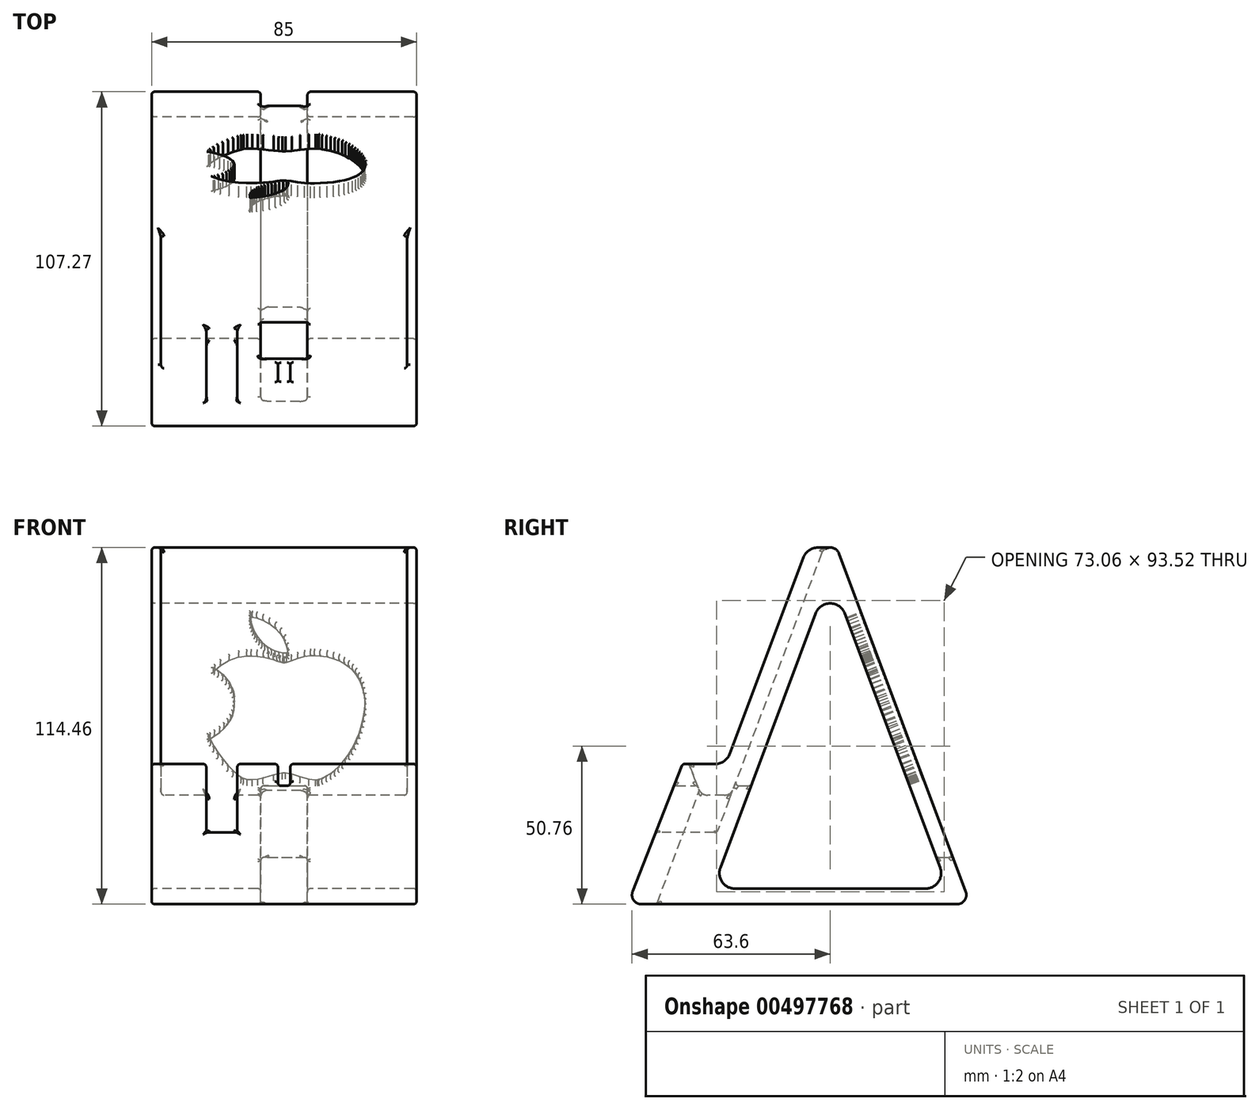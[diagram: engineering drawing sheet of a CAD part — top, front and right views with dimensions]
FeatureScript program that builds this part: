
annotation { "Feature Type Name" : "Feature", "Feature Type Description" : "" }
export const myFeature = defineFeature(function(context is Context, id is Id, definition is map)
    precondition{}
    {
        {
            var Q0;
            Q0=qCreatedBy(makeId("Right.planeOp"),FACE);
            var sketch = newSketch(context, id + "F0", { "sketchPlane" : qUnion([Q0])});
            skLineSegment(sketch, "E0", {"start": v(0, 0) * mm, "end": v(0, 120) * mm, "construction": true});
            skLineSegment(sketch, "E1", {"start": v(0, 0) * mm, "end": v(45, 0) * mm, "construction": true});
            skLineSegment(sketch, "E2", {"start": v(0, 0) * mm, "end": v(-65, 0) * mm, "construction": true});
            skLineSegment(sketch, "E3", {"start": v(-65, 0) * mm, "end": v(-65, 35) * mm, "construction": true});
            skLineSegment(sketch, "E4", {"start": v(2.8, 112.5) * mm, "end": v(43.48, 4.05) * mm});
            skLineSegment(sketch, "E5.MirrorCS", {"start": v(-2.8, 112.5) * mm, "end": v(-31.15, 36.95) * mm});
            skLineSegment(sketch, "E6.0", {"start": v(-16.85, 126.32) * mm, "end": v(-47.35, 45) * mm, "construction": true});
            skLineSegment(sketch, "E7", {"start": v(40.67, 0) * mm, "end": v(-60.6, 0) * mm});
            skLineSegment(sketch, "E8.0", {"start": v(30.57, 5) * mm, "end": v(-30.57, 5) * mm});
            skLineSegment(sketch, "E9.0", {"start": v(4.68, 93.28) * mm, "end": v(35.25, 11.76) * mm});
            skArc(sketch, "E10.filletArc", {"start": v(30.57, 5) * mm, "mid": v(34.68, 7.15) * mm, "end": v(35.25, 11.76) * mm});
            skPoint(sketch, "E11.visualSharp", {"position": v(45, 0) * mm});
            skArc(sketch, "E11.filletArc", {"start": v(40.67, 0) * mm, "mid": v(43.14, 1.3) * mm, "end": v(43.48, 4.05) * mm});
            skPoint(sketch, "E12.visualSharp", {"position": v(0, 120) * mm});
            skArc(sketch, "E12.filletArc", {"start": v(2.8, 112.5) * mm, "mid": v(0, 114.46) * mm, "end": v(-2.8, 112.5) * mm});
            skLineSegment(sketch, "E13.0", {"start": v(-4.68, 93.28) * mm, "end": v(-35.25, 11.76) * mm});
            skArc(sketch, "E14.filletArc", {"start": v(4.68, 93.28) * mm, "mid": v(0, 96.52) * mm, "end": v(-4.68, 93.28) * mm});
            skArc(sketch, "E15.filletArc", {"start": v(-35.25, 11.76) * mm, "mid": v(-34.68, 7.15) * mm, "end": v(-30.57, 5) * mm});
            skLineSegment(sketch, "E16.0", {"start": v(-33.95, 35) * mm, "end": v(-39.38, 35) * mm});
            skPoint(sketch, "E17.orphan", {"position": v(-45, 0) * mm});
            skPoint(sketch, "E18.visualSharp", {"position": v(-31.88, 35) * mm});
            skArc(sketch, "E18.filletArc", {"start": v(-33.95, 35) * mm, "mid": v(-32.25, 35.53) * mm, "end": v(-31.15, 36.95) * mm});
            skLineSegment(sketch, "E19", {"start": v(-47.6, 44.37) * mm, "end": v(-63.4, 4.1) * mm});
            skPoint(sketch, "E20.visualSharp", {"position": v(-65, 0) * mm});
            skArc(sketch, "E20.filletArc", {"start": v(-63.4, 4.1) * mm, "mid": v(-63.08, 1.3) * mm, "end": v(-60.6, 0) * mm});
            skLineSegment(sketch, "E21", {"start": v(-46.67, 45) * mm, "end": v(-46.03, 45) * mm});
            skLineSegment(sketch, "E22", {"start": v(-46.35, 45) * mm, "end": v(-46.35, 35.19) * mm, "construction": true});
            skLineSegment(sketch, "E23.MirrorCS", {"start": v(-45.1, 44.37) * mm, "end": v(-42.17, 36.9) * mm});
            skArc(sketch, "E24.filletArc", {"start": v(-42.17, 36.9) * mm, "mid": v(-41.07, 35.52) * mm, "end": v(-39.38, 35) * mm});
            skPoint(sketch, "E25.visualSharp", {"position": v(-47.35, 45) * mm});
            skArc(sketch, "E25.filletArc", {"start": v(-46.67, 45) * mm, "mid": v(-47.23, 44.83) * mm, "end": v(-47.6, 44.37) * mm});
            skPoint(sketch, "E26.visualSharp", {"position": v(-45.35, 45) * mm});
            skArc(sketch, "E26.filletArc", {"start": v(-45.1, 44.37) * mm, "mid": v(-45.47, 44.83) * mm, "end": v(-46.03, 45) * mm});
            skSolve(sketch);
        }
        {
            var Q0;
            Q0=makeQuery(id+"F0.imprint","IMPRINT",FACE,{"disambiguationData":[TD([[makeQuery(id+"F0.imprint","IMPRINT",EDGE,{"derivedFrom":sQuery(id+"F0.wireOp",EDGE,"E4")}),-1.0]])]});
            extrude(context, id + "F1", {"entities" : qUnion([Q0]), "endBound" : BoundingType.SYMMETRIC, "depth" : 85 * mm});
        }
        {
            var Q0;
            Q0=qCreatedBy(makeId("Right.planeOp"),FACE);
            var sketch = newSketch(context, id + "F2", { "sketchPlane" : qUnion([Q0])});
            skLineSegment(sketch, "E27.0", {"start": v(-4.68, 93.28) * mm, "end": v(-35.25, 11.76) * mm, "construction": true});
            skLineSegment(sketch, "E28.0", {"start": v(-18.73, 98.54) * mm, "end": v(-49.3, 17.02) * mm, "construction": true});
            skLineSegment(sketch, "E29.0", {"start": v(40.67, 0) * mm, "end": v(-60.6, 0) * mm, "construction": true});
            skLineSegment(sketch, "E30.0", {"start": v(40.67, -5) * mm, "end": v(-60.6, -5) * mm, "construction": true});
            skLineSegment(sketch, "E31.0", {"start": v(30.57, 5) * mm, "end": v(-30.57, 5) * mm, "construction": true});
            skLineSegment(sketch, "E32.0", {"start": v(30.57, 15) * mm, "end": v(-30.57, 15) * mm, "construction": true});
            skLineSegment(sketch, "E33", {"start": v(48.4, 22.62) * mm, "end": v(48.4, -8.79) * mm, "construction": true});
            skLineSegment(sketch, "E34.0", {"start": v(-33.95, 35) * mm, "end": v(-39.38, 35) * mm, "construction": true});
            skPoint(sketch, "E34.1", {"position": v(-36.67, 35) * mm});
            skLineSegment(sketch, "E35.0", {"start": v(-33.95, 38) * mm, "end": v(-39.38, 38) * mm, "construction": true});
            skLineSegment(sketch, "E36", {"start": v(-49.3, 17.02) * mm, "end": v(-57.76, -5.55) * mm, "construction": true});
            skLineSegment(sketch, "E37", {"start": v(-33.95, 38) * mm, "end": v(-17.32, 38) * mm, "construction": true});
            skLineSegment(sketch, "E38", {"start": v(-30.57, 15) * mm, "end": v(-21.94, 38) * mm});
            skLineSegment(sketch, "E39", {"start": v(-30.57, 15) * mm, "end": v(48.4, 15) * mm});
            skLineSegment(sketch, "E40", {"start": v(48.4, 15) * mm, "end": v(48.4, -5) * mm});
            skLineSegment(sketch, "E41", {"start": v(48.4, -5) * mm, "end": v(-57.56, -5) * mm});
            skLineSegment(sketch, "E42", {"start": v(-57.56, -5) * mm, "end": v(-41.43, 38) * mm});
            skLineSegment(sketch, "E43", {"start": v(-41.43, 38) * mm, "end": v(-21.94, 38) * mm});
            skSolve(sketch);
        }
        {
            var Q0;
            Q0=makeQuery(id+"F2.imprint","IMPRINT",FACE,{"disambiguationData":[TD([[makeQuery(id+"F2.imprint","IMPRINT",EDGE,{"derivedFrom":sQuery(id+"F2.wireOp",EDGE,"E38")}),1.0]])]});
            extrude(context, id + "F3", {"entities" : qUnion([Q0]), "operationType" : NewBodyOperationType.REMOVE, "endBound" : BoundingType.SYMMETRIC, "depth" : 15 * mm});
        }
        {
            var Q0;
            Q0=qCreatedBy(makeId("Right.planeOp"),FACE);
            cPlane(context, id + "F4", {"entities" : qUnion([Q0]), "cplaneType" : CPlaneType.OFFSET, "offset" : 20 * mm, "oppositeDirection" : true, "width" : 150 * mm, "height" : 150 * mm});
        }
        {
            var Q0;
            Q0=qCreatedBy(id+"F4.planeOp",FACE);
            var sketch = newSketch(context, id + "F5", { "sketchPlane" : qUnion([Q0])});
            skLineSegment(sketch, "E44.0", {"start": v(-33.95, 35) * mm, "end": v(-39.38, 35) * mm, "construction": true});
            skLineSegment(sketch, "E45.0", {"start": v(-33.95, 38) * mm, "end": v(-39.38, 38) * mm, "construction": true});
            skLineSegment(sketch, "E46.0", {"start": v(-33.95, 23) * mm, "end": v(-39.38, 23) * mm, "construction": true});
            skLineSegment(sketch, "E47.0", {"start": v(-2.8, 112.5) * mm, "end": v(-31.15, 36.95) * mm});
            skLineSegment(sketch, "E48", {"start": v(-31.15, 36.95) * mm, "end": v(-36.38, 23) * mm, "construction": true});
            skPoint(sketch, "E48.endSnap0", {"position": v(-36.67, 23) * mm});
            skLineSegment(sketch, "E49", {"start": v(-36.38, 23) * mm, "end": v(-59.4, 23) * mm, "construction": true});
            skLineSegment(sketch, "E50", {"start": v(-59.4, 23) * mm, "end": v(-53.77, 38) * mm, "construction": true});
            skLineSegment(sketch, "E51", {"start": v(-30.75, 38) * mm, "end": v(-31.15, 36.95) * mm, "construction": true});
            skLineSegment(sketch, "E52", {"start": v(-36.38, 23) * mm, "end": v(-59.4, 23) * mm});
            skLineSegment(sketch, "E53", {"start": v(-53.77, 38) * mm, "end": v(-59.4, 23) * mm});
            skLineSegment(sketch, "E54", {"start": v(-30.75, 38) * mm, "end": v(-36.38, 23) * mm});
            skLineSegment(sketch, "E55", {"start": v(-30.75, 38) * mm, "end": v(-39.38, 38) * mm});
            skLineSegment(sketch, "E56", {"start": v(-39.38, 38) * mm, "end": v(-44.36, 49.18) * mm});
            skLineSegment(sketch, "E57", {"start": v(-44.36, 49.18) * mm, "end": v(-50.54, 48.17) * mm});
            skLineSegment(sketch, "E58", {"start": v(-50.54, 48.17) * mm, "end": v(-53.77, 38) * mm});
            skSolve(sketch);
        }
        {
            var Q0;
            {var subQ2=sQuery(id+"F5.wireOp",EDGE,"E52");Q0=makeQuery(id+"F5.imprint","IMPRINT",FACE,{"disambiguationData":[TD([[makeQuery(id+"F5.imprint","IMPRINT",EDGE,{"derivedFrom":subQ2}),-1.0]])]});}
            extrude(context, id + "F6", {"entities" : qUnion([Q0]), "operationType" : NewBodyOperationType.REMOVE, "endBound" : BoundingType.SYMMETRIC, "depth" : 10 * mm});
        }
        {
            var Q0;
            Q0=qCreatedBy(makeId("Front.planeOp"),FACE);
            cPlane(context, id + "F7", {"entities" : qUnion([Q0]), "cplaneType" : CPlaneType.OFFSET, "offset" : 46 * mm, "width" : 150 * mm, "height" : 150 * mm});
        }
        {
            var Q0;
            Q0=qCreatedBy(id+"F7.planeOp",FACE);
            var sketch = newSketch(context, id + "F8", { "sketchPlane" : qUnion([Q0])});
            skLineSegment(sketch, "E59.0", {"start": v(42.5, 45) * mm, "end": v(-15, 45) * mm, "construction": true});
            skLineSegment(sketch, "E60", {"start": v(0, 0) * mm, "end": v(0, 47) * mm, "construction": true});
            skLineSegment(sketch, "E61.0", {"start": v(2, 39) * mm, "end": v(2, 47) * mm});
            skLineSegment(sketch, "E62.0", {"start": v(-2, 39) * mm, "end": v(-2, 47) * mm});
            skLineSegment(sketch, "E63", {"start": v(1, 38) * mm, "end": v(-1, 38) * mm});
            skLineSegment(sketch, "E64", {"start": v(-2, 47) * mm, "end": v(2, 47) * mm});
            skPoint(sketch, "E65.visualSharp", {"position": v(2, 38) * mm});
            skArc(sketch, "E65.filletArc", {"start": v(1, 38) * mm, "mid": v(1.7, 38.3) * mm, "end": v(2, 39) * mm});
            skPoint(sketch, "E66.visualSharp", {"position": v(-2, 38) * mm});
            skArc(sketch, "E66.filletArc", {"start": v(-2, 39) * mm, "mid": v(-1.7, 38.3) * mm, "end": v(-1, 38) * mm});
            skSolve(sketch);
        }
        {
            var Q0;
            Q0=makeQuery(id+"F8.imprint","IMPRINT",FACE,{"disambiguationData":[TD([[makeQuery(id+"F8.imprint","IMPRINT",EDGE,{"derivedFrom":sQuery(id+"F8.wireOp",EDGE,"E61.0")}),1.0]])]});
            extrude(context, id + "F9", {"entities" : qUnion([Q0]), "operationType" : NewBodyOperationType.REMOVE, "endBound" : BoundingType.SYMMETRIC, "depth" : 10 * mm});
        }
        {
            var Q0;
            Q0=makeQuery(id+"F1.opExtrude","SWEPT_FACE",FACE,{"disambiguationData":[OSD([sQuery(id+"F0.wireOp",EDGE,"E4")])]});
            var sketch = newSketch(context, id + "F10", { "sketchPlane" : qUnion([Q0])});
            skLineSegment(sketch, "E67", {"start": v(-10.8, 27.05) * mm, "end": v(-11.15, 27.16) * mm});
            skLineSegment(sketch, "E68", {"start": v(-11.15, 27.16) * mm, "end": v(-12.2, 27.58) * mm});
            skLineSegment(sketch, "E69", {"start": v(-12.2, 27.58) * mm, "end": v(-13.57, 28.3) * mm});
            skLineSegment(sketch, "E70", {"start": v(-13.57, 28.3) * mm, "end": v(-14.9, 29.19) * mm});
            skLineSegment(sketch, "E71", {"start": v(-14.9, 29.19) * mm, "end": v(-16.18, 30.24) * mm});
            skLineSegment(sketch, "E72", {"start": v(-16.18, 30.24) * mm, "end": v(-17.4, 31.45) * mm});
            skLineSegment(sketch, "E73", {"start": v(-17.4, 31.45) * mm, "end": v(-18.58, 32.79) * mm});
            skLineSegment(sketch, "E74", {"start": v(-18.58, 32.79) * mm, "end": v(-19.68, 34.25) * mm});
            skLineSegment(sketch, "E75", {"start": v(-19.68, 34.25) * mm, "end": v(-20.72, 35.82) * mm});
            skLineSegment(sketch, "E76", {"start": v(-20.72, 35.82) * mm, "end": v(-21.68, 37.48) * mm});
            skLineSegment(sketch, "E77", {"start": v(-21.68, 37.48) * mm, "end": v(-22.56, 39.23) * mm});
            skLineSegment(sketch, "E78", {"start": v(-22.56, 39.23) * mm, "end": v(-23.35, 41.05) * mm});
            skLineSegment(sketch, "E79", {"start": v(-23.35, 41.05) * mm, "end": v(-24.04, 42.92) * mm});
            skLineSegment(sketch, "E80", {"start": v(-24.04, 42.92) * mm, "end": v(-24.64, 44.84) * mm});
            skLineSegment(sketch, "E81", {"start": v(-24.64, 44.84) * mm, "end": v(-25.13, 46.78) * mm});
            skLineSegment(sketch, "E82", {"start": v(-25.13, 46.78) * mm, "end": v(-25.51, 48.73) * mm});
            skLineSegment(sketch, "E83", {"start": v(-25.86, 51) * mm, "end": v(-25.51, 48.73) * mm});
            skLineSegment(sketch, "E84", {"start": v(-25.86, 51) * mm, "end": v(-25.92, 52.73) * mm});
            skLineSegment(sketch, "E85", {"start": v(-25.92, 52.73) * mm, "end": v(-25.92, 53.78) * mm});
            skLineSegment(sketch, "E86", {"start": v(-25.92, 54.55) * mm, "end": v(-25.8, 56.43) * mm});
            skLineSegment(sketch, "E87", {"start": v(-25.8, 56.43) * mm, "end": v(-25.53, 58.26) * mm});
            skLineSegment(sketch, "E88", {"start": v(-25.53, 58.26) * mm, "end": v(-25.11, 60.02) * mm});
            skLineSegment(sketch, "E89", {"start": v(-25.11, 60.02) * mm, "end": v(-24.54, 61.7) * mm});
            skLineSegment(sketch, "E90", {"start": v(-24.54, 61.7) * mm, "end": v(-23.82, 63.3) * mm});
            skLineSegment(sketch, "E91", {"start": v(-23.82, 63.3) * mm, "end": v(-22.92, 64.78) * mm});
            skLineSegment(sketch, "E92", {"start": v(-22.92, 64.78) * mm, "end": v(-21.86, 66.14) * mm});
            skLineSegment(sketch, "E93", {"start": v(-21.86, 66.14) * mm, "end": v(-20.62, 67.37) * mm});
            skLineSegment(sketch, "E94", {"start": v(-20.62, 67.37) * mm, "end": v(-19.2, 68.45) * mm});
            skLineSegment(sketch, "E95", {"start": v(-19.2, 68.45) * mm, "end": v(-17.58, 69.38) * mm});
            skLineSegment(sketch, "E96", {"start": v(-17.58, 69.38) * mm, "end": v(-15.78, 70.12) * mm});
            skLineSegment(sketch, "E97", {"start": v(-15.78, 70.12) * mm, "end": v(-13.77, 70.69) * mm});
            skLineSegment(sketch, "E98", {"start": v(-13.77, 70.69) * mm, "end": v(-11.55, 71.05) * mm});
            skLineSegment(sketch, "E99", {"start": v(-11.55, 71.05) * mm, "end": v(-9.73, 71.19) * mm});
            skLineSegment(sketch, "E100", {"start": v(-9.73, 71.19) * mm, "end": v(-9.13, 71.2) * mm});
            skLineSegment(sketch, "E101", {"start": v(-9.13, 71.2) * mm, "end": v(-8.5, 71.2) * mm});
            skLineSegment(sketch, "E102", {"start": v(-8.5, 71.2) * mm, "end": v(-6.6, 70.9) * mm});
            skLineSegment(sketch, "E103", {"start": v(-6.6, 70.9) * mm, "end": v(-4.4, 70.17) * mm});
            skLineSegment(sketch, "E104", {"start": v(-4.4, 70.17) * mm, "end": v(-2.36, 69.34) * mm});
            skLineSegment(sketch, "E105", {"start": v(-2.36, 69.34) * mm, "end": v(-0.84, 68.82) * mm});
            skLineSegment(sketch, "E106", {"start": v(-0.84, 68.82) * mm, "end": v(-0.31, 68.72) * mm});
            skLineSegment(sketch, "E107", {"start": v(-0.31, 68.72) * mm, "end": v(-0.12, 68.69) * mm});
            skLineSegment(sketch, "E108", {"start": v(-0.12, 68.69) * mm, "end": v(0.49, 68.72) * mm});
            skLineSegment(sketch, "E109", {"start": v(0.49, 68.72) * mm, "end": v(1.36, 68.93) * mm});
            skLineSegment(sketch, "E110", {"start": v(1.36, 68.93) * mm, "end": v(2.35, 69.3) * mm});
            skLineSegment(sketch, "E111", {"start": v(2.35, 69.3) * mm, "end": v(3.53, 69.74) * mm});
            skLineSegment(sketch, "E112", {"start": v(3.53, 69.74) * mm, "end": v(4.95, 70.2) * mm});
            skLineSegment(sketch, "E113", {"start": v(4.95, 70.2) * mm, "end": v(6.66, 70.63) * mm});
            skLineSegment(sketch, "E114", {"start": v(6.66, 70.63) * mm, "end": v(8.73, 70.93) * mm});
            skLineSegment(sketch, "E115", {"start": v(8.73, 70.93) * mm, "end": v(10.58, 71.04) * mm});
            skLineSegment(sketch, "E116", {"start": v(10.58, 71.04) * mm, "end": v(11.2, 71.04) * mm});
            skLineSegment(sketch, "E117", {"start": v(11.2, 71.04) * mm, "end": v(12.03, 71.04) * mm});
            skLineSegment(sketch, "E118", {"start": v(12.03, 71.04) * mm, "end": v(14.53, 70.65) * mm});
            skLineSegment(sketch, "E119", {"start": v(14.53, 70.65) * mm, "end": v(17.6, 69.53) * mm});
            skLineSegment(sketch, "E120", {"start": v(17.6, 69.53) * mm, "end": v(20.32, 67.77) * mm});
            skLineSegment(sketch, "E121", {"start": v(20.32, 67.77) * mm, "end": v(22.12, 66.09) * mm});
            skLineSegment(sketch, "E122", {"start": v(22.12, 66.09) * mm, "end": v(22.63, 65.46) * mm});
            skLineSegment(sketch, "E123", {"start": v(21.03, 64.3) * mm, "end": v(22.22, 65.19) * mm});
            skLineSegment(sketch, "E124", {"start": v(21.03, 64.3) * mm, "end": v(19.64, 63.01) * mm});
            skLineSegment(sketch, "E125", {"start": v(19.64, 63.01) * mm, "end": v(18.46, 61.63) * mm});
            skLineSegment(sketch, "E126", {"start": v(18.46, 61.63) * mm, "end": v(17.5, 60.18) * mm});
            skLineSegment(sketch, "E127", {"start": v(17.5, 60.18) * mm, "end": v(16.75, 58.66) * mm});
            skLineSegment(sketch, "E128", {"start": v(16.75, 58.66) * mm, "end": v(16.23, 57.1) * mm});
            skLineSegment(sketch, "E129", {"start": v(16.23, 57.1) * mm, "end": v(15.94, 55.5) * mm});
            skLineSegment(sketch, "E130", {"start": v(15.94, 55.5) * mm, "end": v(15.88, 53.88) * mm});
            skLineSegment(sketch, "E131", {"start": v(15.88, 53.88) * mm, "end": v(16.05, 52.27) * mm});
            skLineSegment(sketch, "E132", {"start": v(16.05, 52.27) * mm, "end": v(16.46, 50.68) * mm});
            skLineSegment(sketch, "E133", {"start": v(16.46, 50.68) * mm, "end": v(17.12, 49.13) * mm});
            skLineSegment(sketch, "E134", {"start": v(17.12, 49.13) * mm, "end": v(18.02, 47.63) * mm});
            skLineSegment(sketch, "E135", {"start": v(18.02, 47.63) * mm, "end": v(19.18, 46.2) * mm});
            skLineSegment(sketch, "E136", {"start": v(19.18, 46.2) * mm, "end": v(20.59, 44.85) * mm});
            skLineSegment(sketch, "E137", {"start": v(20.59, 44.85) * mm, "end": v(22.26, 43.6) * mm});
            skLineSegment(sketch, "E138", {"start": v(22.26, 43.6) * mm, "end": v(23.7, 42.73) * mm});
            skLineSegment(sketch, "E139", {"start": v(23.7, 42.73) * mm, "end": v(24.2, 42.47) * mm});
            skLineSegment(sketch, "E140", {"start": v(24.2, 42.47) * mm, "end": v(24.08, 42) * mm});
            skLineSegment(sketch, "E141", {"start": v(24.08, 42) * mm, "end": v(23.56, 40.6) * mm});
            skLineSegment(sketch, "E142", {"start": v(23.56, 40.6) * mm, "end": v(22.53, 38.48) * mm});
            skLineSegment(sketch, "E143", {"start": v(22.53, 38.48) * mm, "end": v(21.19, 36.24) * mm});
            skLineSegment(sketch, "E144", {"start": v(21.19, 36.24) * mm, "end": v(19.65, 34) * mm});
            skLineSegment(sketch, "E145", {"start": v(19.65, 34) * mm, "end": v(18, 31.9) * mm});
            skLineSegment(sketch, "E146", {"start": v(18, 31.9) * mm, "end": v(16.35, 30.07) * mm});
            skLineSegment(sketch, "E147", {"start": v(16.35, 30.07) * mm, "end": v(14.78, 28.63) * mm});
            skLineSegment(sketch, "E148", {"start": v(14.78, 28.63) * mm, "end": v(13.77, 27.88) * mm});
            skLineSegment(sketch, "E149", {"start": v(13.77, 27.88) * mm, "end": v(13.4, 27.7) * mm});
            skLineSegment(sketch, "E150", {"start": v(13.4, 27.7) * mm, "end": v(13.03, 27.51) * mm});
            skLineSegment(sketch, "E151", {"start": v(13.03, 27.51) * mm, "end": v(11.82, 27.18) * mm});
            skLineSegment(sketch, "E152", {"start": v(11.82, 27.18) * mm, "end": v(10.18, 27.08) * mm});
            skLineSegment(sketch, "E153", {"start": v(10.18, 27.08) * mm, "end": v(8.49, 27.3) * mm});
            skLineSegment(sketch, "E154", {"start": v(8.49, 27.3) * mm, "end": v(6.78, 27.73) * mm});
            skLineSegment(sketch, "E155", {"start": v(6.78, 27.73) * mm, "end": v(5.08, 28.26) * mm});
            skLineSegment(sketch, "E156", {"start": v(5.08, 28.26) * mm, "end": v(3.4, 28.79) * mm});
            skLineSegment(sketch, "E157", {"start": v(3.4, 28.79) * mm, "end": v(1.77, 29.2) * mm});
            skLineSegment(sketch, "E158", {"start": v(1.77, 29.2) * mm, "end": v(0.6, 29.4) * mm});
            skLineSegment(sketch, "E159", {"start": v(0.6, 29.4) * mm, "end": v(0.22, 29.4) * mm});
            skLineSegment(sketch, "E160", {"start": v(0.22, 29.4) * mm, "end": v(-0.45, 29.43) * mm});
            skLineSegment(sketch, "E161", {"start": v(-0.45, 29.43) * mm, "end": v(-2.5, 29.04) * mm});
            skLineSegment(sketch, "E162", {"start": v(-2.5, 29.04) * mm, "end": v(-5.22, 28.14) * mm});
            skLineSegment(sketch, "E163", {"start": v(-5.22, 28.14) * mm, "end": v(-7.98, 27.3) * mm});
            skLineSegment(sketch, "E164", {"start": v(-7.98, 27.3) * mm, "end": v(-10.1, 26.99) * mm});
            skLineSegment(sketch, "E165", {"start": v(-10.1, 26.99) * mm, "end": v(-10.8, 27.05) * mm});
            skLineSegment(sketch, "E166", {"start": v(-1.12, 70.55) * mm, "end": v(-0.78, 70.53) * mm});
            skLineSegment(sketch, "E167", {"start": v(-0.78, 70.53) * mm, "end": v(0.27, 70.58) * mm});
            skLineSegment(sketch, "E168", {"start": v(0.27, 70.58) * mm, "end": v(1.6, 70.8) * mm});
            skLineSegment(sketch, "E169", {"start": v(1.6, 70.8) * mm, "end": v(2.86, 71.18) * mm});
            skLineSegment(sketch, "E170", {"start": v(2.86, 71.18) * mm, "end": v(4.04, 71.73) * mm});
            skLineSegment(sketch, "E171", {"start": v(4.04, 71.73) * mm, "end": v(5.14, 72.42) * mm});
            skLineSegment(sketch, "E172", {"start": v(5.14, 72.42) * mm, "end": v(6.17, 73.22) * mm});
            skLineSegment(sketch, "E173", {"start": v(6.17, 73.22) * mm, "end": v(7.1, 74.13) * mm});
            skLineSegment(sketch, "E174", {"start": v(7.1, 74.13) * mm, "end": v(7.94, 75.14) * mm});
            skLineSegment(sketch, "E175", {"start": v(7.94, 75.14) * mm, "end": v(8.68, 76.2) * mm});
            skLineSegment(sketch, "E176", {"start": v(8.68, 76.2) * mm, "end": v(9.32, 77.34) * mm});
            skLineSegment(sketch, "E177", {"start": v(9.32, 77.34) * mm, "end": v(9.85, 78.5) * mm});
            skLineSegment(sketch, "E178", {"start": v(9.85, 78.5) * mm, "end": v(10.27, 79.7) * mm});
            skLineSegment(sketch, "E179", {"start": v(10.27, 79.7) * mm, "end": v(10.57, 80.89) * mm});
            skLineSegment(sketch, "E180", {"start": v(10.57, 80.89) * mm, "end": v(10.75, 82.07) * mm});
            skLineSegment(sketch, "E181", {"start": v(10.75, 82.07) * mm, "end": v(10.8, 83.23) * mm});
            skLineSegment(sketch, "E182", {"start": v(10.8, 83.23) * mm, "end": v(10.77, 84.06) * mm});
            skLineSegment(sketch, "E183", {"start": v(10.77, 84.06) * mm, "end": v(10.73, 84.34) * mm});
            skLineSegment(sketch, "E184", {"start": v(10.73, 84.34) * mm, "end": v(10.25, 84.3) * mm});
            skLineSegment(sketch, "E185", {"start": v(10.25, 84.3) * mm, "end": v(8.84, 83.98) * mm});
            skLineSegment(sketch, "E186", {"start": v(8.84, 83.98) * mm, "end": v(6.8, 83.23) * mm});
            skLineSegment(sketch, "E187", {"start": v(6.8, 83.23) * mm, "end": v(4.77, 82.08) * mm});
            skLineSegment(sketch, "E188", {"start": v(4.77, 82.08) * mm, "end": v(2.85, 80.53) * mm});
            skLineSegment(sketch, "E189", {"start": v(2.85, 80.53) * mm, "end": v(1.17, 78.6) * mm});
            skLineSegment(sketch, "E190", {"start": v(1.17, 78.6) * mm, "end": v(-0.13, 76.3) * mm});
            skLineSegment(sketch, "E191", {"start": v(-0.13, 76.3) * mm, "end": v(-0.94, 73.61) * mm});
            skLineSegment(sketch, "E192", {"start": v(-0.94, 73.61) * mm, "end": v(-1.16, 71.3) * mm});
            skLineSegment(sketch, "E193", {"start": v(-1.16, 71.3) * mm, "end": v(-1.12, 70.55) * mm});
            skLineSegment(sketch, "E194", {"start": v(0, 0) * mm, "end": v(0, 101.3) * mm, "construction": true});
            skLineSegment(sketch, "E195", {"start": v(-25.92, 54.55) * mm, "end": v(-25.92, 53.78) * mm});
            skLineSegment(sketch, "E196", {"start": v(22.22, 65.19) * mm, "end": v(22.63, 65.46) * mm});
            skSolve(sketch);
        }
        {
            var Q0;
            Q0 = qSketchRegion(id + "F10", true);
            extrude(context, id + "F11", {"entities" : qUnion([Q0]), "operationType" : NewBodyOperationType.REMOVE, "oppositeDirection" : true, "depth" : 7 * mm});
        }
        {
            var Q0;
            Q0=makeQuery(id+"F1.opExtrude","CAP_FACE",FACE,{"disambiguationData":[OSD([sQuery(id+"F0.wireOp",EDGE,"E4"),sQuery(id+"F0.wireOp",EDGE,"E5.MirrorCS"),sQuery(id+"F0.wireOp",EDGE,"E7"),sQuery(id+"F0.wireOp",EDGE,"E8.0"),sQuery(id+"F0.wireOp",EDGE,"E9.0"),sQuery(id+"F0.wireOp",EDGE,"E10.filletArc"),sQuery(id+"F0.wireOp",EDGE,"E11.filletArc"),sQuery(id+"F0.wireOp",EDGE,"E12.filletArc"),sQuery(id+"F0.wireOp",EDGE,"E13.0"),sQuery(id+"F0.wireOp",EDGE,"E14.filletArc"),sQuery(id+"F0.wireOp",EDGE,"E15.filletArc"),sQuery(id+"F0.wireOp",EDGE,"E16.0"),sQuery(id+"F0.wireOp",EDGE,"E18.filletArc"),sQuery(id+"F0.wireOp",EDGE,"E19"),sQuery(id+"F0.wireOp",EDGE,"E20.filletArc"),sQuery(id+"F0.wireOp",EDGE,"E21"),sQuery(id+"F0.wireOp",EDGE,"E23.MirrorCS"),sQuery(id+"F0.wireOp",EDGE,"E24.filletArc"),sQuery(id+"F0.wireOp",EDGE,"E25.filletArc"),sQuery(id+"F0.wireOp",EDGE,"E26.filletArc")])],"isStart":false});
            var sketch = newSketch(context, id + "F12", { "sketchPlane" : qUnion([Q0])});
            skLineSegment(sketch, "E197.0", {"start": v(-2.8, 112.5) * mm, "end": v(-31.15, 36.95) * mm});
            skLineSegment(sketch, "E198.0", {"start": v(-46.67, 45) * mm, "end": v(-46.03, 45) * mm, "construction": true});
            skLineSegment(sketch, "E199", {"start": v(-46.03, 45) * mm, "end": v(-33.47, 45) * mm});
            skArc(sketch, "E200.0", {"start": v(0, 114.46) * mm, "mid": v(-1.7, 113.92) * mm, "end": v(-2.8, 112.5) * mm});
            skLineSegment(sketch, "E201", {"start": v(0, 114.46) * mm, "end": v(-7.42, 114.46) * mm});
            skLineSegment(sketch, "E202.0", {"start": v(-45.1, 44.37) * mm, "end": v(-42.17, 36.9) * mm});
            skArc(sketch, "E203.0", {"start": v(-45.1, 44.37) * mm, "mid": v(-45.47, 44.83) * mm, "end": v(-46.03, 45) * mm});
            skArc(sketch, "E204.0", {"start": v(-42.17, 36.9) * mm, "mid": v(-41.07, 35.52) * mm, "end": v(-39.38, 35) * mm});
            skLineSegment(sketch, "E205.0", {"start": v(-33.95, 35) * mm, "end": v(-39.38, 35) * mm});
            skArc(sketch, "E206.0", {"start": v(-33.95, 35) * mm, "mid": v(-32.25, 35.53) * mm, "end": v(-31.15, 36.95) * mm});
            skPoint(sketch, "E207.orphan", {"position": v(2.8, 112.5) * mm});
            skLineSegment(sketch, "E208", {"start": v(-33.47, 45) * mm, "end": v(-7.42, 114.46) * mm});
            skSolve(sketch);
        }
        {
            var Q0;
            Q0=makeQuery(id+"F12.imprint","IMPRINT",FACE,{"disambiguationData":[TD([[makeQuery(id+"F12.imprint","IMPRINT",EDGE,{"derivedFrom":sQuery(id+"F12.wireOp",EDGE,"E197.0")}),-1.0]])]});
            extrude(context, id + "F13", {"entities" : qUnion([Q0]), "operationType" : NewBodyOperationType.ADD, "oppositeDirection" : true, "depth" : 3 * mm});
        }
        {
            var Q0;
            Q0=qCreatedBy(makeId("Right.planeOp"),FACE);
            cPlane(context, id + "F14", {"entities" : qUnion([Q0]), "cplaneType" : CPlaneType.OFFSET, "offset" : 42.5 * mm, "oppositeDirection" : true, "width" : 150 * mm, "height" : 150 * mm});
        }
        {
            var Q0;
            Q0=qCreatedBy(id+"F14.planeOp",FACE);
            var sketch = newSketch(context, id + "F15", { "sketchPlane" : qUnion([Q0])});
            skLineSegment(sketch, "E209.0", {"start": v(0, 114.46) * mm, "end": v(-7.42, 114.46) * mm});
            skArc(sketch, "E210.0", {"start": v(0, 114.46) * mm, "mid": v(-1.7, 113.92) * mm, "end": v(-2.8, 112.5) * mm});
            skLineSegment(sketch, "E211.0", {"start": v(-2.8, 112.5) * mm, "end": v(-31.15, 36.95) * mm});
            skLineSegment(sketch, "E212.0", {"start": v(-33.47, 45) * mm, "end": v(-7.42, 114.46) * mm});
            skArc(sketch, "E213.0", {"start": v(-33.95, 35) * mm, "mid": v(-32.25, 35.53) * mm, "end": v(-31.15, 36.95) * mm});
            skLineSegment(sketch, "E214.0", {"start": v(-33.95, 35) * mm, "end": v(-39.38, 35) * mm});
            skArc(sketch, "E215.0", {"start": v(-42.17, 36.9) * mm, "mid": v(-41.07, 35.52) * mm, "end": v(-39.38, 35) * mm});
            skLineSegment(sketch, "E216.0", {"start": v(-45.1, 44.37) * mm, "end": v(-42.17, 36.9) * mm});
            skArc(sketch, "E217.0", {"start": v(-45.1, 44.37) * mm, "mid": v(-45.47, 44.83) * mm, "end": v(-46.03, 45) * mm});
            skLineSegment(sketch, "E218", {"start": v(-33.47, 45) * mm, "end": v(-33.83, 45) * mm});
            skLineSegment(sketch, "E219", {"start": v(-43.52, 45) * mm, "end": v(-33.83, 45) * mm});
            skLineSegment(sketch, "E220", {"start": v(-46.03, 45) * mm, "end": v(-43.52, 45) * mm});
            skSolve(sketch);
        }
        {
            var Q0;
            Q0=makeQuery(id+"F15.imprint","IMPRINT",FACE,{"disambiguationData":[TD([[makeQuery(id+"F15.imprint","IMPRINT",EDGE,{"derivedFrom":sQuery(id+"F15.wireOp",EDGE,"E209.0")}),1.0]])]});
            extrude(context, id + "F16", {"entities" : qUnion([Q0]), "operationType" : NewBodyOperationType.ADD, "depth" : 3 * mm});
        }
        {
            var Q0;
            Q0=makeQuery(id+"F13.opExtrude","SWEPT_EDGE",EDGE,{"disambiguationData":[OSD([sQuery(id+"F12.wireOp",EDGE,"E199"),sQuery(id+"F12.wireOp",EDGE,"E208")])]});
            var Q1;
            Q1=makeQuery(id+"F16.opExtrude","SWEPT_EDGE",EDGE,{"disambiguationData":[OSD([sQuery(id+"F15.wireOp",EDGE,"E212.0"),sQuery(id+"F15.wireOp",EDGE,"E218")])]});
            var Q2;
            Q2=makeQuery(id+"F13.opExtrude","SWEPT_EDGE",EDGE,{"disambiguationData":[OSD([sQuery(id+"F12.wireOp",EDGE,"E201"),sQuery(id+"F12.wireOp",EDGE,"E208")])]});
            var Q3;
            Q3=makeQuery(id+"F16.opExtrude","SWEPT_EDGE",EDGE,{"disambiguationData":[OSD([sQuery(id+"F15.wireOp",EDGE,"E209.0"),sQuery(id+"F15.wireOp",EDGE,"E212.0")])]});
            fillet(context, id + "F17", {"entities" : qUnion([Q0, Q1, Q2, Q3]), "radius" : 5 * mm, "tangentPropagation" : true, "allowEdgeOverflow" : false});
        }
        {
            var Q0;
            Q0=makeQuery(id+"F16.opExtrude","CAP_EDGE",EDGE,{"disambiguationData":[OSD([sQuery(id+"F15.wireOp",EDGE,"E216.0")])],"isStart":false});
            var Q1;
            Q1=makeQuery(id+"F13.opExtrude","CAP_EDGE",EDGE,{"disambiguationData":[OSD([sQuery(id+"F12.wireOp",EDGE,"E197.0")])],"isStart":false});
            var Q2;
            Q2=makeQuery(id+"F3.boolean.opBoolean","INTERSECT",EDGE,{"derivedFrom":[makeQuery(id+"F1.opExtrude","SWEPT_FACE",FACE,{"disambiguationData":[OSD([sQuery(id+"F0.wireOp",EDGE,"E5.MirrorCS")])]}),makeQuery(id+"F3.opExtrude","SWEPT_FACE",FACE,{"disambiguationData":[OSD([sQuery(id+"F2.wireOp",EDGE,"E43")])]})]});
            var Q3;
            Q3=makeQuery(id+"F3.boolean.opBoolean","INTERSECT",EDGE,{"derivedFrom":[makeQuery(id+"F1.opExtrude","SWEPT_FACE",FACE,{"disambiguationData":[OSD([sQuery(id+"F0.wireOp",EDGE,"E18.filletArc")])]}),makeQuery(id+"F3.opExtrude","CAP_FACE",FACE,{"disambiguationData":[OSD([sQuery(id+"F2.wireOp",EDGE,"E38"),sQuery(id+"F2.wireOp",EDGE,"E39"),sQuery(id+"F2.wireOp",EDGE,"E40"),sQuery(id+"F2.wireOp",EDGE,"E41"),sQuery(id+"F2.wireOp",EDGE,"E42"),sQuery(id+"F2.wireOp",EDGE,"E43")])],"isStart":true})]});
            var Q4;
            Q4=makeQuery(id+"F3.boolean.opBoolean","INTERSECT",EDGE,{"derivedFrom":[makeQuery(id+"F1.opExtrude","SWEPT_FACE",FACE,{"disambiguationData":[OSD([sQuery(id+"F0.wireOp",EDGE,"E16.0")])]}),makeQuery(id+"F3.opExtrude","CAP_FACE",FACE,{"disambiguationData":[OSD([sQuery(id+"F2.wireOp",EDGE,"E38"),sQuery(id+"F2.wireOp",EDGE,"E39"),sQuery(id+"F2.wireOp",EDGE,"E40"),sQuery(id+"F2.wireOp",EDGE,"E41"),sQuery(id+"F2.wireOp",EDGE,"E42"),sQuery(id+"F2.wireOp",EDGE,"E43")])],"isStart":false})]});
            var Q5;
            {var subQ2=sQuery(id+"F0.wireOp",EDGE,"E16.0");Q5=makeQuery(id+"F6.boolean.opBoolean","INTERSECT",EDGE,{"derivedFrom":[makeQuery(id+"F3.boolean.opBoolean","SPLIT",FACE,{"disambiguationData":[TD([makeQuery(id+"F3.opExtrude","CAP_FACE",FACE,{"disambiguationData":[OSD([sQuery(id+"F2.wireOp",EDGE,"E38"),sQuery(id+"F2.wireOp",EDGE,"E39"),sQuery(id+"F2.wireOp",EDGE,"E40"),sQuery(id+"F2.wireOp",EDGE,"E41"),sQuery(id+"F2.wireOp",EDGE,"E42"),sQuery(id+"F2.wireOp",EDGE,"E43")])],"isStart":true})])],"derivedFrom":makeQuery(id+"F1.opExtrude","SWEPT_FACE",FACE,{"disambiguationData":[OSD([subQ2])]})}),makeQuery(id+"F6.opExtrude","CAP_FACE",FACE,{"disambiguationData":[OSD([sQuery(id+"F5.wireOp",EDGE,"E52"),sQuery(id+"F5.wireOp",EDGE,"E53"),sQuery(id+"F5.wireOp",EDGE,"E54"),sQuery(id+"F5.wireOp",EDGE,"E55"),sQuery(id+"F5.wireOp",EDGE,"E56"),sQuery(id+"F5.wireOp",EDGE,"E57"),sQuery(id+"F5.wireOp",EDGE,"E58")])],"isStart":false})]});}
            var Q6;
            Q6=makeQuery(id+"F6.boolean.opBoolean","COPY",EDGE,{"derivedFrom":makeQuery(id+"F6.opExtrude","CAP_EDGE",EDGE,{"disambiguationData":[OSD([sQuery(id+"F5.wireOp",EDGE,"E54")])],"isStart":false})});
            var Q7;
            Q7=makeQuery(id+"F6.boolean.opBoolean","COPY",EDGE,{"derivedFrom":makeQuery(id+"F6.opExtrude","SWEPT_EDGE",EDGE,{"disambiguationData":[OSD([sQuery(id+"F5.wireOp",EDGE,"E52"),sQuery(id+"F5.wireOp",EDGE,"E54")])]})});
            var Q8;
            Q8=makeQuery(id+"F6.boolean.opBoolean","COPY",EDGE,{"derivedFrom":makeQuery(id+"F6.opExtrude","CAP_EDGE",EDGE,{"disambiguationData":[OSD([sQuery(id+"F5.wireOp",EDGE,"E54")])],"isStart":true})});
            var Q9;
            {var subQ2=sQuery(id+"F0.wireOp",EDGE,"E16.0");Q9=makeQuery(id+"F6.boolean.opBoolean","INTERSECT",EDGE,{"derivedFrom":[makeQuery(id+"F3.boolean.opBoolean","SPLIT",FACE,{"disambiguationData":[TD([makeQuery(id+"F3.opExtrude","CAP_FACE",FACE,{"disambiguationData":[OSD([sQuery(id+"F2.wireOp",EDGE,"E38"),sQuery(id+"F2.wireOp",EDGE,"E39"),sQuery(id+"F2.wireOp",EDGE,"E40"),sQuery(id+"F2.wireOp",EDGE,"E41"),sQuery(id+"F2.wireOp",EDGE,"E42"),sQuery(id+"F2.wireOp",EDGE,"E43")])],"isStart":true})])],"derivedFrom":makeQuery(id+"F1.opExtrude","SWEPT_FACE",FACE,{"disambiguationData":[OSD([subQ2])]})}),makeQuery(id+"F6.opExtrude","CAP_FACE",FACE,{"disambiguationData":[OSD([sQuery(id+"F5.wireOp",EDGE,"E52"),sQuery(id+"F5.wireOp",EDGE,"E53"),sQuery(id+"F5.wireOp",EDGE,"E54"),sQuery(id+"F5.wireOp",EDGE,"E55"),sQuery(id+"F5.wireOp",EDGE,"E56"),sQuery(id+"F5.wireOp",EDGE,"E57"),sQuery(id+"F5.wireOp",EDGE,"E58")])],"isStart":true})]});}
            var Q10;
            Q10=makeQuery(id+"F6.boolean.opBoolean","INTERSECT",EDGE,{"derivedFrom":[makeQuery(id+"F1.opExtrude","SWEPT_FACE",FACE,{"disambiguationData":[OSD([sQuery(id+"F0.wireOp",EDGE,"E19")])]}),makeQuery(id+"F6.opExtrude","SWEPT_FACE",FACE,{"disambiguationData":[OSD([sQuery(id+"F5.wireOp",EDGE,"E52")])]})]});
            var Q11;
            Q11=makeQuery(id+"F9.boolean.opBoolean","INTERSECT",EDGE,{"derivedFrom":[makeQuery(id+"F1.opExtrude","SWEPT_FACE",FACE,{"disambiguationData":[OSD([sQuery(id+"F0.wireOp",EDGE,"E19")])]}),makeQuery(id+"F9.opExtrude","SWEPT_FACE",FACE,{"disambiguationData":[OSD([sQuery(id+"F8.wireOp",EDGE,"E62.0")])]})]});
            var Q12;
            Q12=makeQuery(id+"F3.boolean.opBoolean","COPY",FACE,{"derivedFrom":makeQuery(id+"F3.opExtrude","CAP_FACE",FACE,{"disambiguationData":[OSD([sQuery(id+"F2.wireOp",EDGE,"E38"),sQuery(id+"F2.wireOp",EDGE,"E39"),sQuery(id+"F2.wireOp",EDGE,"E40"),sQuery(id+"F2.wireOp",EDGE,"E41"),sQuery(id+"F2.wireOp",EDGE,"E42"),sQuery(id+"F2.wireOp",EDGE,"E43")])],"isStart":false})});
            var Q13;
            Q13=makeQuery(id+"F3.boolean.opBoolean","COPY",FACE,{"derivedFrom":makeQuery(id+"F3.opExtrude","CAP_FACE",FACE,{"disambiguationData":[OSD([sQuery(id+"F2.wireOp",EDGE,"E38"),sQuery(id+"F2.wireOp",EDGE,"E39"),sQuery(id+"F2.wireOp",EDGE,"E40"),sQuery(id+"F2.wireOp",EDGE,"E41"),sQuery(id+"F2.wireOp",EDGE,"E42"),sQuery(id+"F2.wireOp",EDGE,"E43")])],"isStart":true})});
            var Q14;
            Q14=makeQuery(id+"F16.opExtrude","CAP_FACE",FACE,{"disambiguationData":[OSD([sQuery(id+"F15.wireOp",EDGE,"E209.0"),sQuery(id+"F15.wireOp",EDGE,"E210.0"),sQuery(id+"F15.wireOp",EDGE,"E211.0"),sQuery(id+"F15.wireOp",EDGE,"E212.0"),sQuery(id+"F15.wireOp",EDGE,"E213.0"),sQuery(id+"F15.wireOp",EDGE,"E214.0"),sQuery(id+"F15.wireOp",EDGE,"E215.0"),sQuery(id+"F15.wireOp",EDGE,"E216.0"),sQuery(id+"F15.wireOp",EDGE,"E217.0"),sQuery(id+"F15.wireOp",EDGE,"E218"),sQuery(id+"F15.wireOp",EDGE,"E219"),sQuery(id+"F15.wireOp",EDGE,"E220")])],"isStart":false});
            var Q15;
            Q15=makeQuery(id+"F13.opExtrude","CAP_FACE",FACE,{"disambiguationData":[OSD([sQuery(id+"F12.wireOp",EDGE,"E197.0"),sQuery(id+"F12.wireOp",EDGE,"E199"),sQuery(id+"F12.wireOp",EDGE,"E200.0"),sQuery(id+"F12.wireOp",EDGE,"E201"),sQuery(id+"F12.wireOp",EDGE,"E202.0"),sQuery(id+"F12.wireOp",EDGE,"E203.0"),sQuery(id+"F12.wireOp",EDGE,"E204.0"),sQuery(id+"F12.wireOp",EDGE,"E205.0"),sQuery(id+"F12.wireOp",EDGE,"E206.0"),sQuery(id+"F12.wireOp",EDGE,"E208")])],"isStart":false});
            var Q16;
            Q16=makeQuery(id+"F13.boolean.opBoolean","MERGE",FACE,{"derivedFrom":[makeQuery(id+"F1.opExtrude","CAP_FACE",FACE,{"disambiguationData":[OSD([sQuery(id+"F0.wireOp",EDGE,"E4"),sQuery(id+"F0.wireOp",EDGE,"E5.MirrorCS"),sQuery(id+"F0.wireOp",EDGE,"E7"),sQuery(id+"F0.wireOp",EDGE,"E8.0"),sQuery(id+"F0.wireOp",EDGE,"E9.0"),sQuery(id+"F0.wireOp",EDGE,"E10.filletArc"),sQuery(id+"F0.wireOp",EDGE,"E11.filletArc"),sQuery(id+"F0.wireOp",EDGE,"E12.filletArc"),sQuery(id+"F0.wireOp",EDGE,"E13.0"),sQuery(id+"F0.wireOp",EDGE,"E14.filletArc"),sQuery(id+"F0.wireOp",EDGE,"E15.filletArc"),sQuery(id+"F0.wireOp",EDGE,"E16.0"),sQuery(id+"F0.wireOp",EDGE,"E18.filletArc"),sQuery(id+"F0.wireOp",EDGE,"E19"),sQuery(id+"F0.wireOp",EDGE,"E20.filletArc"),sQuery(id+"F0.wireOp",EDGE,"E21"),sQuery(id+"F0.wireOp",EDGE,"E23.MirrorCS"),sQuery(id+"F0.wireOp",EDGE,"E24.filletArc"),sQuery(id+"F0.wireOp",EDGE,"E25.filletArc"),sQuery(id+"F0.wireOp",EDGE,"E26.filletArc")])],"isStart":false}),makeQuery(id+"F13.opExtrude","CAP_FACE",FACE,{"disambiguationData":[OSD([sQuery(id+"F12.wireOp",EDGE,"E197.0"),sQuery(id+"F12.wireOp",EDGE,"E199"),sQuery(id+"F12.wireOp",EDGE,"E200.0"),sQuery(id+"F12.wireOp",EDGE,"E201"),sQuery(id+"F12.wireOp",EDGE,"E202.0"),sQuery(id+"F12.wireOp",EDGE,"E203.0"),sQuery(id+"F12.wireOp",EDGE,"E204.0"),sQuery(id+"F12.wireOp",EDGE,"E205.0"),sQuery(id+"F12.wireOp",EDGE,"E206.0"),sQuery(id+"F12.wireOp",EDGE,"E208")])],"isStart":true})]});
            var Q17;
            Q17=makeQuery(id+"F16.boolean.opBoolean","MERGE",FACE,{"derivedFrom":[makeQuery(id+"F1.opExtrude","CAP_FACE",FACE,{"disambiguationData":[OSD([sQuery(id+"F0.wireOp",EDGE,"E4"),sQuery(id+"F0.wireOp",EDGE,"E5.MirrorCS"),sQuery(id+"F0.wireOp",EDGE,"E7"),sQuery(id+"F0.wireOp",EDGE,"E8.0"),sQuery(id+"F0.wireOp",EDGE,"E9.0"),sQuery(id+"F0.wireOp",EDGE,"E10.filletArc"),sQuery(id+"F0.wireOp",EDGE,"E11.filletArc"),sQuery(id+"F0.wireOp",EDGE,"E12.filletArc"),sQuery(id+"F0.wireOp",EDGE,"E13.0"),sQuery(id+"F0.wireOp",EDGE,"E14.filletArc"),sQuery(id+"F0.wireOp",EDGE,"E15.filletArc"),sQuery(id+"F0.wireOp",EDGE,"E16.0"),sQuery(id+"F0.wireOp",EDGE,"E18.filletArc"),sQuery(id+"F0.wireOp",EDGE,"E19"),sQuery(id+"F0.wireOp",EDGE,"E20.filletArc"),sQuery(id+"F0.wireOp",EDGE,"E21"),sQuery(id+"F0.wireOp",EDGE,"E23.MirrorCS"),sQuery(id+"F0.wireOp",EDGE,"E24.filletArc"),sQuery(id+"F0.wireOp",EDGE,"E25.filletArc"),sQuery(id+"F0.wireOp",EDGE,"E26.filletArc")])],"isStart":true}),makeQuery(id+"F16.opExtrude","CAP_FACE",FACE,{"disambiguationData":[OSD([sQuery(id+"F15.wireOp",EDGE,"E209.0"),sQuery(id+"F15.wireOp",EDGE,"E210.0"),sQuery(id+"F15.wireOp",EDGE,"E211.0"),sQuery(id+"F15.wireOp",EDGE,"E212.0"),sQuery(id+"F15.wireOp",EDGE,"E213.0"),sQuery(id+"F15.wireOp",EDGE,"E214.0"),sQuery(id+"F15.wireOp",EDGE,"E215.0"),sQuery(id+"F15.wireOp",EDGE,"E216.0"),sQuery(id+"F15.wireOp",EDGE,"E217.0"),sQuery(id+"F15.wireOp",EDGE,"E218"),sQuery(id+"F15.wireOp",EDGE,"E219"),sQuery(id+"F15.wireOp",EDGE,"E220")])],"isStart":true})]});
            fillet(context, id + "F18", {"entities" : qUnion([Q0, Q1, Q2, Q3, Q4, Q5, Q6, Q7, Q8, Q9, Q10, Q11, Q12, Q13, Q14, Q15, Q16, Q17]), "radius" : 1 * mm, "tangentPropagation" : true, "allowEdgeOverflow" : false});
        }
        {
            var Q0;
            Q0=makeQuery(id+"F1.opExtrude","SWEPT_FACE",FACE,{"disambiguationData":[OSD([sQuery(id+"F0.wireOp",EDGE,"E4")])]});
            var Q1;
            Q1=makeQuery(id+"F1.opExtrude","SWEPT_FACE",FACE,{"disambiguationData":[OSD([sQuery(id+"F0.wireOp",EDGE,"E9.0")])]});
            var Q2;
            Q2=makeQuery(id+"F6.boolean.opBoolean","COPY",FACE,{"derivedFrom":makeQuery(id+"F6.opExtrude","SWEPT_FACE",FACE,{"disambiguationData":[OSD([sQuery(id+"F5.wireOp",EDGE,"E52")])]})});
            fillet(context, id + "F19", {"entities" : qUnion([Q0, Q1, Q2]), "radius" : .5 * mm, "tangentPropagation" : true, "allowEdgeOverflow" : false});
        }
    });
